# Revit family: Emergency_Equipment-Haws_Corporation-Laboratory_Eyewash_7612 new
name_source: partatom
category: Plumbing Fixtures
revit_build: Autodesk Revit Architecture 2015 (Build: 20160512_1515(x64)
units: mm (PartAtom-declared; Revit-internal decimal feet)

## types (1)
- 7612
    Arm Length = 12 1/4"
    Assembly Code = D2010610
    CWFU = 1
    Cost = 0 $
    Cost Note = For Cost information please visit the Resource tab in the Product Page URL
    Description = Dust covers allow to stay protected from debris when not in use
    Duct Covers = Plastic - Haws Corporation - Yellow Dust Cover - 9091
    Flow = 6 GPM
    HWFU = 1
    Head Height = 8 3/8"
    Keynote = 15400
    Manufacturer = Haws Corporation
    Max. Thick = 1 1/8"
    Metal = Metal - Haws Corporation - High Polished Stainless Steel
    Model = 7612
    Product Documentation Link = https://www.hawsco.com
    Product Page URL = http://www.hawsco.com
    Series = Twin Soft-Flo™ heads
    Supply Radius = 1/4"
    Swing Arms = Metal - Haws Corporation - High Polished Stainless Steel
    Type Comments = Lab units are installed in accessible sink locations
    URL = http://www.hawsco.com
    Version = 2014-v2.0a
    WFU = 1

## geometry (parser evidence)
native form markers: Blend x28, Sweep x2
no freeform markers — native parametric forms only
